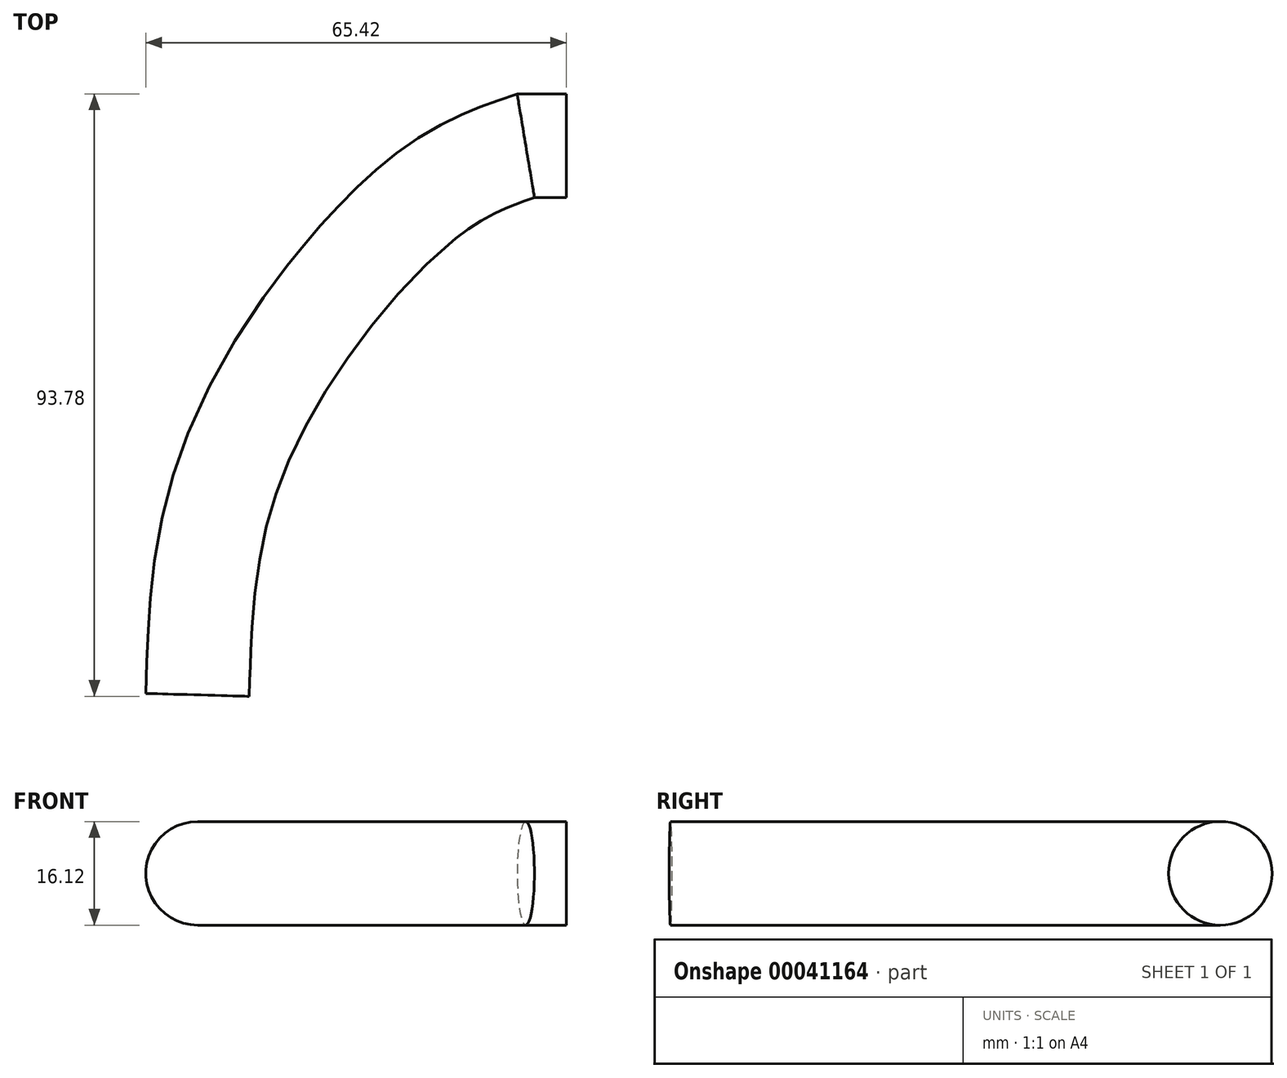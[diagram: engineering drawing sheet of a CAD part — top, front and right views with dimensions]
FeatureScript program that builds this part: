
annotation { "Feature Type Name" : "Feature", "Feature Type Description" : "" }
export const myFeature = defineFeature(function(context is Context, id is Id, definition is map)
    precondition{}
    {
        {
            var Q0;
            Q0=qCreatedBy(makeId("Top.planeOp"),FACE);
            var sketch = newSketch(context, id + "F0", { "sketchPlane" : qUnion([Q0])});
            skFitSpline(sketch, "E0", {"points": [v(-57.36, -59.02) * mm, v(-51.06, -20.5) * mm, v(-22.22, 18.35) * mm, v(-6.3, 26.49) * mm], "startDerivative": vector(2.95, 104.97) * mm, "endDerivative": vector(61.3, 20.94) * mm});
            skFitSpline(sketch, "E1", {"points": [v(-6.3, 26.49) * mm, v(0, 26.49) * mm], "startDerivative": vector(6.3, 0) * mm, "endDerivative": vector(6.3, 0) * mm});
            skSolve(sketch);
        }
        {
            var Q0;
            Q0=qCreatedBy(makeId("Right.planeOp"),FACE);
            var sketch = newSketch(context, id + "F1", { "sketchPlane" : qUnion([Q0])});
            skCircle(sketch, "E2", {"center": v(26.49, 0) * mm, "radius": 8.06 * mm});
            skSolve(sketch);
        }
        {
            var Q0;
            Q0=makeQuery(id+"F1.imprint","IMPRINT",FACE,{"disambiguationData":[TD([[makeQuery(id+"F1.imprint","IMPRINT",EDGE,{"derivedFrom":sQuery(id+"F1.wireOp",EDGE,"E2")}),1.0]])]});
            var Q1;
            Q1=sQuery(id+"F0.wireOp",EDGE,"E0");
            var Q2;
            Q2=sQuery(id+"F0.wireOp",EDGE,"E1");
            sweep(context, id + "F2", {"profiles" : qUnion([Q0]), "path" : qUnion([Q1, Q2])});
        }
    });
